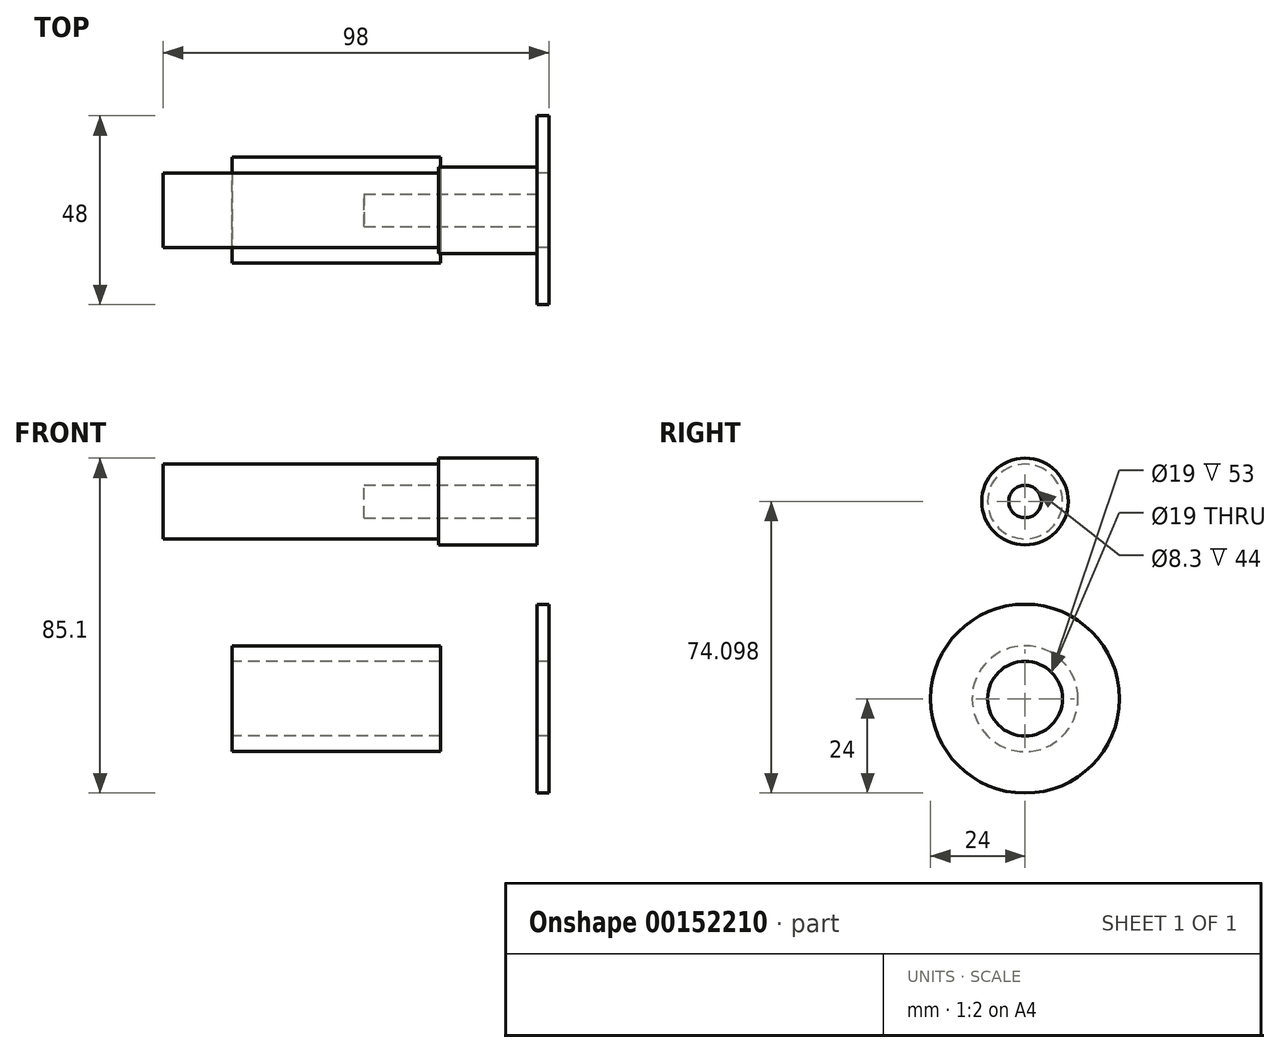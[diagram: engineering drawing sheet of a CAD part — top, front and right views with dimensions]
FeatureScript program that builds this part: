
annotation { "Feature Type Name" : "Feature", "Feature Type Description" : "" }
export const myFeature = defineFeature(function(context is Context, id is Id, definition is map)
    precondition{}
    {
        {
            var Q0;
            Q0=qCreatedBy(makeId("Right.planeOp"),FACE);
            var sketch = newSketch(context, id + "F0", { "sketchPlane" : qUnion([Q0])});
            skCircle(sketch, "E0", {"center": v(0, 0) * mm, "radius": 9.5 * mm});
            skCircle(sketch, "E1", {"center": v(0, 0) * mm, "radius": 24 * mm});
            skSolve(sketch);
        }
        {
            var Q0;
            Q0=qSketchRegion(id+"F0",true);
            extrude(context, id + "F1", {"entities" : qUnion([Q0]), "depth" : 3 * mm});
        }
        {
            var Q0;
            Q0=qCreatedBy(makeId("Front.planeOp"),FACE);
            var sketch = newSketch(context, id + "F2", { "sketchPlane" : qUnion([Q0])});
            skLineSegment(sketch, "E2", {"start": v(55.65, 0) * mm, "end": v(-77.5, 0) * mm, "construction": true});
            skSolve(sketch);
        }
        {
            var Q0;
            Q0=sQuery(id+"F2.wireOp",VERTEX,"E2.end");
            var Q1;
            Q1=qCreatedBy(makeId("Right.planeOp"),FACE);
            cPlane(context, id + "F3", {"entities" : qUnion([Q0, Q1]), "cplaneType" : CPlaneType.PLANE_POINT, "offset" : 25 * mm, "width" : 150 * mm, "height" : 150 * mm});
        }
        {
            var Q0;
            Q0=qCreatedBy(id+"F3.planeOp",FACE);
            var sketch = newSketch(context, id + "F4", { "sketchPlane" : qUnion([Q0])});
            skCircle(sketch, "E3", {"center": v(0, 0) * mm, "radius": 9.5 * mm});
            skCircle(sketch, "E4", {"center": v(0, 0) * mm, "radius": 13.45 * mm});
            skSolve(sketch);
        }
        {
            var Q0;
            Q0=qSketchRegion(id+"F4",true);
            extrude(context, id + "F5", {"entities" : qUnion([Q0]), "depth" : 53 * mm});
        }
        {
            var Q0;
            Q0=qCreatedBy(makeId("Right.planeOp"),FACE);
            var sketch = newSketch(context, id + "F6", { "sketchPlane" : qUnion([Q0])});
            skCircle(sketch, "E5", {"center": v(0, 50.1) * mm, "radius": 11 * mm});
            skSolve(sketch);
        }
        {
            var Q0;
            Q0=qSketchRegion(id+"F6",true);
            extrude(context, id + "F7", {"entities" : qUnion([Q0]), "oppositeDirection" : true, "depth" : 25 * mm});
        }
        {
            var Q0;
            Q0=makeQuery(id+"F7.opExtrude","CAP_FACE",FACE,{"disambiguationData":[OSD([sQuery(id+"F6.wireOp",EDGE,"E5")])],"isStart":false});
            var sketch = newSketch(context, id + "F8", { "sketchPlane" : qUnion([Q0])});
            skCircle(sketch, "E6", {"center": v(0, 50.1) * mm, "radius": 9.5 * mm});
            skSolve(sketch);
        }
        {
            var Q0;
            Q0=qSketchRegion(id+"F8",true);
            extrude(context, id + "F9", {"entities" : qUnion([Q0]), "operationType" : NewBodyOperationType.ADD, "depth" : 70 * mm});
        }
        {
            var Q0;
            Q0=makeQuery(id+"F7.opExtrude","CAP_FACE",FACE,{"disambiguationData":[OSD([sQuery(id+"F6.wireOp",EDGE,"E5")])],"isStart":true});
            var sketch = newSketch(context, id + "F10", { "sketchPlane" : qUnion([Q0])});
            skCircle(sketch, "E7", {"center": v(0, 50.1) * mm, "radius": 4.15 * mm});
            skSolve(sketch);
        }
        {
            var Q0;
            Q0=qSketchRegion(id+"F10",true);
            extrude(context, id + "F11", {"entities" : qUnion([Q0]), "operationType" : NewBodyOperationType.REMOVE, "oppositeDirection" : true, "depth" : 44 * mm});
        }
    });
